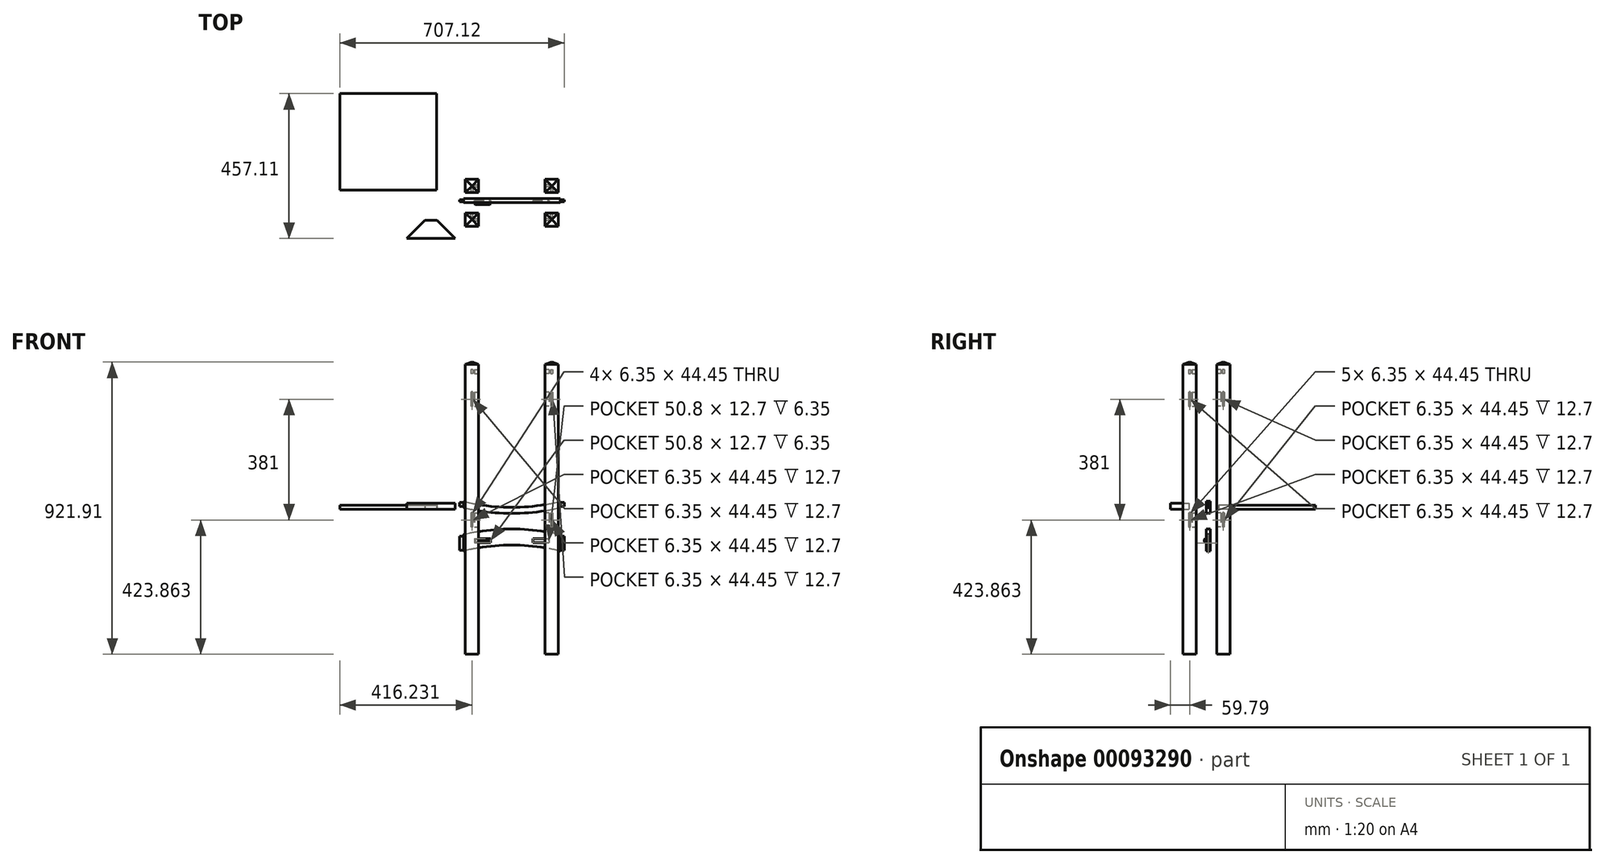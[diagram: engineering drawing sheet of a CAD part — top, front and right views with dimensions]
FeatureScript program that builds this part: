
annotation { "Feature Type Name" : "Feature", "Feature Type Description" : "" }
export const myFeature = defineFeature(function(context is Context, id is Id, definition is map)
    precondition{}
    {
        {
            var Q0;
            Q0=qCreatedBy(makeId("Front.planeOp"),FACE);
            var sketch = newSketch(context, id + "F0", { "sketchPlane" : qUnion([Q0])});
            skLineSegment(sketch, "E0.left", {"start": v(-165.1, 22.23) * mm, "end": v(-165.1, 9.53) * mm});
            skLineSegment(sketch, "E0.right", {"start": v(165.1, 22.23) * mm, "end": v(165.1, 9.53) * mm});
            skLineSegment(sketch, "E1", {"start": v(-152.4, 25.4) * mm, "end": v(-152.4, 22.23) * mm});
            skLineSegment(sketch, "E2", {"start": v(152.4, 25.4) * mm, "end": v(152.4, 22.23) * mm});
            skLineSegment(sketch, "E3.bottom", {"start": v(-165.1, 22.23) * mm, "end": v(-152.4, 22.23) * mm});
            skLineSegment(sketch, "E3.top", {"start": v(-165.1, 9.53) * mm, "end": v(-152.4, 9.53) * mm});
            skLineSegment(sketch, "E4.bottom", {"start": v(165.1, 22.23) * mm, "end": v(152.4, 22.23) * mm});
            skLineSegment(sketch, "E4.top", {"start": v(165.1, 9.53) * mm, "end": v(152.4, 9.53) * mm});
            skLineSegment(sketch, "E5.trimOffspring", {"start": v(-152.4, 9.53) * mm, "end": v(-152.4, 5.76) * mm});
            skPoint(sketch, "E6.orphan", {"position": v(-165.1, -25.4) * mm});
            skLineSegment(sketch, "E7.trimOffspring", {"start": v(152.4, 9.53) * mm, "end": v(152.4, 5.76) * mm});
            skLineSegment(sketch, "E8", {"start": v(-154.76, 6.35) * mm, "end": v(154.76, 6.35) * mm, "construction": true});
            skLineSegment(sketch, "E9", {"start": v(0, 25.4) * mm, "end": v(0, -25.4) * mm, "construction": true});
            skPoint(sketch, "E10", {"position": v(0, 6.35) * mm});
            skArc(sketch, "E11", {"start": v(-152.4, 25.4) * mm, "mid": v(0, 6.35) * mm, "end": v(152.4, 25.4) * mm});
            skArc(sketch, "E12.trimOffspring", {"start": v(-152.4, 5.76) * mm, "mid": v(0, -12.7) * mm, "end": v(152.4, 5.76) * mm});
            skPoint(sketch, "E13.orphan", {"position": v(-152.4, -25.4) * mm});
            skPoint(sketch, "E14.orphan", {"position": v(152.4, -25.4) * mm});
            skSolve(sketch);
        }
        {
            var Q0;
            Q0=qSketchRegion(id+"F0",true);
            extrude(context, id + "F1", {"entities" : qUnion([Q0]), "oppositeDirection" : true, "depth" : 12.7 * mm});
        }
        {
            var Q0;
            Q0=qCreatedBy(makeId("Front.planeOp"),FACE);
            var sketch = newSketch(context, id + "F2", { "sketchPlane" : qUnion([Q0])});
            skLineSegment(sketch, "E15.left", {"start": v(-165.1, -84.02) * mm, "end": v(-165.1, -128.47) * mm});
            skLineSegment(sketch, "E15.right", {"start": v(165.1, -84.02) * mm, "end": v(165.1, -128.47) * mm});
            skLineSegment(sketch, "E16", {"start": v(-152.4, -79.36) * mm, "end": v(-152.4, -84.02) * mm});
            skLineSegment(sketch, "E17", {"start": v(152.4, -79.36) * mm, "end": v(152.4, -84.02) * mm});
            skLineSegment(sketch, "E18", {"start": v(152.4, -84.02) * mm, "end": v(165.1, -84.02) * mm});
            skLineSegment(sketch, "E19", {"start": v(152.4, -128.47) * mm, "end": v(165.1, -128.47) * mm});
            skLineSegment(sketch, "E20", {"start": v(-165.1, -128.47) * mm, "end": v(-152.4, -128.47) * mm});
            skLineSegment(sketch, "E21", {"start": v(-165.1, -84.02) * mm, "end": v(-152.4, -84.02) * mm});
            skPoint(sketch, "E22.orphan", {"position": v(165.1, -131.64) * mm});
            skLineSegment(sketch, "E23.0", {"start": v(-152.4, -112.6) * mm, "end": v(152.4, -112.6) * mm, "construction": true});
            skLineSegment(sketch, "E24", {"start": v(0, -112.6) * mm, "end": v(0, -131.64) * mm, "construction": true});
            skArc(sketch, "E25", {"start": v(152.4, -131.64) * mm, "mid": v(0, -112.6) * mm, "end": v(-152.4, -131.64) * mm});
            skArc(sketch, "E26.0", {"start": v(152.4, -79.36) * mm, "mid": v(0, -61.8) * mm, "end": v(-152.4, -79.36) * mm});
            skLineSegment(sketch, "E27.trimOffspring", {"start": v(-152.4, -128.47) * mm, "end": v(-152.4, -131.64) * mm});
            skLineSegment(sketch, "E28.trimOffspring", {"start": v(152.4, -128.47) * mm, "end": v(152.4, -131.64) * mm});
            skSolve(sketch);
        }
        {
            var Q0;
            Q0=qSketchRegion(id+"F2",true);
            extrude(context, id + "F3", {"entities" : qUnion([Q0]), "oppositeDirection" : true, "depth" : 12.7 * mm});
        }
        {
            var Q0;
            Q0=makeQuery(id+"F3.opExtrude","CAP_FACE",FACE,{"disambiguationData":[OSD([sQuery(id+"F2.wireOp",EDGE,"E15.left"),sQuery(id+"F2.wireOp",EDGE,"E15.right"),sQuery(id+"F2.wireOp",EDGE,"E16"),sQuery(id+"F2.wireOp",EDGE,"E17"),sQuery(id+"F2.wireOp",EDGE,"E18"),sQuery(id+"F2.wireOp",EDGE,"E19"),sQuery(id+"F2.wireOp",EDGE,"E20"),sQuery(id+"F2.wireOp",EDGE,"E21"),sQuery(id+"F2.wireOp",EDGE,"E25"),sQuery(id+"F2.wireOp",EDGE,"E26.0"),sQuery(id+"F2.wireOp",EDGE,"E27.trimOffspring"),sQuery(id+"F2.wireOp",EDGE,"E28.trimOffspring")])],"isStart":true});
            var sketch = newSketch(context, id + "F4", { "sketchPlane" : qUnion([Q0])});
            skLineSegment(sketch, "E29.bottom", {"start": v(-117.47, -91.95) * mm, "end": v(-66.67, -91.95) * mm});
            skLineSegment(sketch, "E29.top", {"start": v(-117.47, -104.65) * mm, "end": v(-66.67, -104.65) * mm});
            skLineSegment(sketch, "E29.left", {"start": v(-117.47, -91.95) * mm, "end": v(-117.47, -104.65) * mm});
            skLineSegment(sketch, "E29.right", {"start": v(-66.67, -91.95) * mm, "end": v(-66.67, -104.65) * mm});
            skPoint(sketch, "E30.oppositeSnap0", {"position": v(-92.07, -104.65) * mm});
            skLineSegment(sketch, "E30.bottom", {"start": v(66.68, -91.95) * mm, "end": v(117.48, -91.95) * mm});
            skLineSegment(sketch, "E30.top", {"start": v(66.68, -104.65) * mm, "end": v(117.48, -104.65) * mm});
            skLineSegment(sketch, "E30.left", {"start": v(66.68, -91.95) * mm, "end": v(66.68, -104.65) * mm});
            skLineSegment(sketch, "E30.right", {"start": v(117.48, -91.95) * mm, "end": v(117.48, -104.65) * mm});
            skSolve(sketch);
        }
        {
            var Q0;
            Q0=qSketchRegion(id+"F4",true);
            extrude(context, id + "F5", {"entities" : qUnion([Q0]), "operationType" : NewBodyOperationType.REMOVE, "oppositeDirection" : true, "depth" : 6.35 * mm});
        }
        {
            var Q0;
            Q0=qCreatedBy(makeId("Top.planeOp"),FACE);
            var sketch = newSketch(context, id + "F6", { "sketchPlane" : qUnion([Q0])});
            skLineSegment(sketch, "E31.bottom", {"start": v(-146.43, -32.48) * mm, "end": v(-105.15, -32.48) * mm});
            skLineSegment(sketch, "E31.top", {"start": v(-146.43, -73.76) * mm, "end": v(-105.15, -73.76) * mm});
            skLineSegment(sketch, "E31.left", {"start": v(-146.43, -32.48) * mm, "end": v(-146.43, -73.76) * mm});
            skLineSegment(sketch, "E31.right", {"start": v(-105.15, -32.48) * mm, "end": v(-105.15, -73.76) * mm});
            skSolve(sketch);
        }
        {
            var Q0;
            Q0=qSketchRegion(id+"F6",true);
            extrude(context, id + "F7", {"entities" : qUnion([Q0]), "endBound" : BoundingType.SYMMETRIC, "depth" : 914.4 * mm});
        }
        {
            var Q0;
            Q0=makeQuery(id+"F7.opExtrude","SWEPT_FACE",FACE,{"disambiguationData":[OSD([sQuery(id+"F6.wireOp",EDGE,"E31.right")])]});
            var sketch = newSketch(context, id + "F8", { "sketchPlane" : qUnion([Q0])});
            skLineSegment(sketch, "E32.bottom", {"start": v(-56.3, 441.33) * mm, "end": v(-49.94, 441.33) * mm});
            skLineSegment(sketch, "E32.top", {"start": v(-56.3, 428.63) * mm, "end": v(-49.94, 428.63) * mm});
            skLineSegment(sketch, "E32.left", {"start": v(-56.3, 441.33) * mm, "end": v(-56.3, 428.63) * mm});
            skLineSegment(sketch, "E32.right", {"start": v(-49.94, 441.33) * mm, "end": v(-49.94, 428.63) * mm});
            skLineSegment(sketch, "E33.bottom", {"start": v(-56.3, 369.89) * mm, "end": v(-49.94, 369.89) * mm});
            skLineSegment(sketch, "E33.top", {"start": v(-56.3, 325.44) * mm, "end": v(-49.94, 325.44) * mm});
            skLineSegment(sketch, "E33.left", {"start": v(-56.3, 369.89) * mm, "end": v(-56.3, 325.44) * mm});
            skLineSegment(sketch, "E33.right", {"start": v(-49.94, 369.89) * mm, "end": v(-49.94, 325.44) * mm});
            skLineSegment(sketch, "E34.bottom", {"start": v(-56.3, -11.11) * mm, "end": v(-49.94, -11.11) * mm});
            skLineSegment(sketch, "E34.top", {"start": v(-56.3, -55.56) * mm, "end": v(-49.94, -55.56) * mm});
            skLineSegment(sketch, "E34.left", {"start": v(-56.3, -11.11) * mm, "end": v(-56.3, -55.56) * mm});
            skLineSegment(sketch, "E34.right", {"start": v(-49.94, -11.11) * mm, "end": v(-49.94, -55.56) * mm});
            skPoint(sketch, "E35", {"position": v(-53.12, 441.33) * mm});
            skSolve(sketch);
        }
        {
            var Q0;
            Q0=makeQuery(id+"F7.opExtrude","CAP_FACE",FACE,{"disambiguationData":[OSD([sQuery(id+"F6.wireOp",EDGE,"E31.bottom"),sQuery(id+"F6.wireOp",EDGE,"E31.top"),sQuery(id+"F6.wireOp",EDGE,"E31.left"),sQuery(id+"F6.wireOp",EDGE,"E31.right")])],"isStart":false});
            extrude(context, id + "F9", {"entities" : qUnion([Q0]), "operationType" : NewBodyOperationType.ADD, "depth" : 7.94 * mm, "hasDraft" : true, "draftAngle" : 70 * degree, "draftPullDirection" : true});
        }
        {
            var Q0;
            Q0=makeQuery(id+"F7.opExtrude","SWEPT_FACE",FACE,{"disambiguationData":[OSD([sQuery(id+"F6.wireOp",EDGE,"E31.bottom")])]});
            var sketch = newSketch(context, id + "F10", { "sketchPlane" : qUnion([Q0])});
            skLineSegment(sketch, "E36.bottom", {"start": v(122.61, 441.33) * mm, "end": v(128.96, 441.33) * mm});
            skLineSegment(sketch, "E36.top", {"start": v(122.61, 428.63) * mm, "end": v(128.96, 428.63) * mm});
            skLineSegment(sketch, "E36.left", {"start": v(122.61, 441.33) * mm, "end": v(122.61, 428.63) * mm});
            skLineSegment(sketch, "E36.right", {"start": v(128.96, 441.33) * mm, "end": v(128.96, 428.63) * mm});
            skLineSegment(sketch, "E37.bottom", {"start": v(122.61, 369.89) * mm, "end": v(128.96, 369.89) * mm});
            skLineSegment(sketch, "E37.top", {"start": v(122.61, 325.44) * mm, "end": v(128.96, 325.44) * mm});
            skLineSegment(sketch, "E37.left", {"start": v(122.61, 369.89) * mm, "end": v(122.61, 325.44) * mm});
            skLineSegment(sketch, "E37.right", {"start": v(128.96, 369.89) * mm, "end": v(128.96, 325.44) * mm});
            skLineSegment(sketch, "E38.bottom", {"start": v(122.61, -11.11) * mm, "end": v(128.96, -11.11) * mm});
            skLineSegment(sketch, "E38.top", {"start": v(122.61, -55.56) * mm, "end": v(128.96, -55.56) * mm});
            skLineSegment(sketch, "E38.left", {"start": v(122.61, -11.11) * mm, "end": v(122.61, -55.56) * mm});
            skLineSegment(sketch, "E38.right", {"start": v(128.96, -11.11) * mm, "end": v(128.96, -55.56) * mm});
            skPoint(sketch, "E39", {"position": v(125.79, 441.33) * mm});
            skLineSegment(sketch, "E40", {"start": v(125.79, 457.2) * mm, "end": v(125.79, 391.14) * mm, "construction": true});
            skSolve(sketch);
        }
        {
            var Q0;
            Q0=makeQuery(id+"F1.opExtrude","CAP_FACE",FACE,{"disambiguationData":[OSD([sQuery(id+"F0.wireOp",EDGE,"E1"),sQuery(id+"F0.wireOp",EDGE,"E2"),sQuery(id+"F0.wireOp",EDGE,"E3.bottom"),sQuery(id+"F0.wireOp",EDGE,"E3.top"),sQuery(id+"F0.wireOp",EDGE,"E0.left"),sQuery(id+"F0.wireOp",EDGE,"E4.bottom"),sQuery(id+"F0.wireOp",EDGE,"E4.top"),sQuery(id+"F0.wireOp",EDGE,"E0.right"),sQuery(id+"F0.wireOp",EDGE,"E5.trimOffspring"),sQuery(id+"F0.wireOp",EDGE,"E7.trimOffspring"),sQuery(id+"F0.wireOp",EDGE,"E11"),sQuery(id+"F0.wireOp",EDGE,"E12.trimOffspring")])],"isStart":true});
            var sketch = newSketch(context, id + "F11", { "sketchPlane" : qUnion([Q0])});
            skLineSegment(sketch, "E41", {"start": v(152.4, 22.23) * mm, "end": v(152.4, 9.53) * mm});
            skLineSegment(sketch, "E42", {"start": v(-152.4, 22.23) * mm, "end": v(-152.4, 9.53) * mm});
            skSolve(sketch);
        }
        {
            var Q0;
            Q0=qSketchRegion(id+"F10",true);
            extrude(context, id + "F12", {"entities" : qUnion([Q0]), "operationType" : NewBodyOperationType.REMOVE, "oppositeDirection" : true, "depth" : 12.7 * mm});
        }
        {
            var Q0;
            Q0=makeQuery(id+"F11.imprint","IMPRINT",FACE,{"disambiguationData":[TD([[makeQuery(id+"F11.imprint","IMPRINT",EDGE,{"derivedFrom":sQuery(id+"F11.wireOp",EDGE,"E42")}),-1.0]])]});
            var Q1;
            Q1=makeQuery(id+"F11.imprint","IMPRINT",FACE,{"disambiguationData":[TD([[makeQuery(id+"F11.imprint","IMPRINT",EDGE,{"derivedFrom":sQuery(id+"F11.wireOp",EDGE,"E41")}),1.0]])]});
            extrude(context, id + "F13", {"entities" : qUnion([Q0, Q1]), "operationType" : NewBodyOperationType.REMOVE, "oppositeDirection" : true, "depth" : 3.17 * mm});
        }
        {
            var Q0;
            Q0=makeQuery(id+"F1.opExtrude","CAP_FACE",FACE,{"disambiguationData":[OSD([sQuery(id+"F0.wireOp",EDGE,"E1"),sQuery(id+"F0.wireOp",EDGE,"E2"),sQuery(id+"F0.wireOp",EDGE,"E3.bottom"),sQuery(id+"F0.wireOp",EDGE,"E3.top"),sQuery(id+"F0.wireOp",EDGE,"E0.left"),sQuery(id+"F0.wireOp",EDGE,"E4.bottom"),sQuery(id+"F0.wireOp",EDGE,"E4.top"),sQuery(id+"F0.wireOp",EDGE,"E0.right"),sQuery(id+"F0.wireOp",EDGE,"E5.trimOffspring"),sQuery(id+"F0.wireOp",EDGE,"E7.trimOffspring"),sQuery(id+"F0.wireOp",EDGE,"E11"),sQuery(id+"F0.wireOp",EDGE,"E12.trimOffspring")])],"isStart":false});
            var sketch = newSketch(context, id + "F14", { "sketchPlane" : qUnion([Q0])});
            skLineSegment(sketch, "E43", {"start": v(-152.4, 22.23) * mm, "end": v(-152.4, 9.53) * mm});
            skLineSegment(sketch, "E44", {"start": v(152.4, 22.23) * mm, "end": v(152.4, 9.53) * mm});
            skSolve(sketch);
        }
        {
            var Q0;
            Q0=makeQuery(id+"F14.imprint","IMPRINT",FACE,{"disambiguationData":[TD([[makeQuery(id+"F14.imprint","IMPRINT",EDGE,{"derivedFrom":sQuery(id+"F14.wireOp",EDGE,"E43")}),-1.0]])]});
            var Q1;
            Q1=makeQuery(id+"F14.imprint","IMPRINT",FACE,{"disambiguationData":[TD([[makeQuery(id+"F14.imprint","IMPRINT",EDGE,{"derivedFrom":sQuery(id+"F14.wireOp",EDGE,"E44")}),1.0]])]});
            extrude(context, id + "F15", {"entities" : qUnion([Q0, Q1]), "operationType" : NewBodyOperationType.REMOVE, "oppositeDirection" : true, "depth" : 3.17 * mm});
        }
        {
            var Q0;
            Q0=makeQuery(id+"F3.opExtrude","CAP_FACE",FACE,{"disambiguationData":[OSD([sQuery(id+"F2.wireOp",EDGE,"E15.left"),sQuery(id+"F2.wireOp",EDGE,"E15.right"),sQuery(id+"F2.wireOp",EDGE,"E16"),sQuery(id+"F2.wireOp",EDGE,"E17"),sQuery(id+"F2.wireOp",EDGE,"E18"),sQuery(id+"F2.wireOp",EDGE,"E19"),sQuery(id+"F2.wireOp",EDGE,"E20"),sQuery(id+"F2.wireOp",EDGE,"E21"),sQuery(id+"F2.wireOp",EDGE,"E25"),sQuery(id+"F2.wireOp",EDGE,"E26.0"),sQuery(id+"F2.wireOp",EDGE,"E27.trimOffspring"),sQuery(id+"F2.wireOp",EDGE,"E28.trimOffspring")])],"isStart":false});
            var sketch = newSketch(context, id + "F16", { "sketchPlane" : qUnion([Q0])});
            skLineSegment(sketch, "E45", {"start": v(-152.4, -84.02) * mm, "end": v(-152.4, -128.47) * mm});
            skLineSegment(sketch, "E46", {"start": v(152.4, -84.02) * mm, "end": v(152.4, -128.47) * mm});
            skSolve(sketch);
        }
        {
            var Q0;
            Q0=makeQuery(id+"F16.imprint","IMPRINT",FACE,{"disambiguationData":[TD([[makeQuery(id+"F16.imprint","IMPRINT",EDGE,{"derivedFrom":sQuery(id+"F16.wireOp",EDGE,"E45")}),-1.0]])]});
            var Q1;
            Q1=makeQuery(id+"F16.imprint","IMPRINT",FACE,{"disambiguationData":[TD([[makeQuery(id+"F16.imprint","IMPRINT",EDGE,{"derivedFrom":sQuery(id+"F16.wireOp",EDGE,"E46")}),1.0]])]});
            extrude(context, id + "F17", {"entities" : qUnion([Q0, Q1]), "operationType" : NewBodyOperationType.REMOVE, "oppositeDirection" : true, "depth" : 3.17 * mm});
        }
        {
            var Q0;
            Q0=makeQuery(id+"F3.opExtrude","CAP_FACE",FACE,{"disambiguationData":[OSD([sQuery(id+"F2.wireOp",EDGE,"E15.left"),sQuery(id+"F2.wireOp",EDGE,"E15.right"),sQuery(id+"F2.wireOp",EDGE,"E16"),sQuery(id+"F2.wireOp",EDGE,"E17"),sQuery(id+"F2.wireOp",EDGE,"E18"),sQuery(id+"F2.wireOp",EDGE,"E19"),sQuery(id+"F2.wireOp",EDGE,"E20"),sQuery(id+"F2.wireOp",EDGE,"E21"),sQuery(id+"F2.wireOp",EDGE,"E25"),sQuery(id+"F2.wireOp",EDGE,"E26.0"),sQuery(id+"F2.wireOp",EDGE,"E27.trimOffspring"),sQuery(id+"F2.wireOp",EDGE,"E28.trimOffspring")])],"isStart":true});
            var sketch = newSketch(context, id + "F18", { "sketchPlane" : qUnion([Q0])});
            skLineSegment(sketch, "E47", {"start": v(-152.4, -84.02) * mm, "end": v(-152.4, -128.47) * mm});
            skLineSegment(sketch, "E48", {"start": v(152.4, -84.02) * mm, "end": v(152.4, -128.47) * mm});
            skSolve(sketch);
        }
        {
            var Q0;
            Q0=makeQuery(id+"F18.imprint","IMPRINT",FACE,{"disambiguationData":[TD([[makeQuery(id+"F18.imprint","IMPRINT",EDGE,{"derivedFrom":sQuery(id+"F18.wireOp",EDGE,"E47")}),-1.0]])]});
            var Q1;
            Q1=makeQuery(id+"F18.imprint","IMPRINT",FACE,{"disambiguationData":[TD([[makeQuery(id+"F18.imprint","IMPRINT",EDGE,{"derivedFrom":sQuery(id+"F18.wireOp",EDGE,"E48")}),1.0]])]});
            extrude(context, id + "F19", {"entities" : qUnion([Q0, Q1]), "operationType" : NewBodyOperationType.REMOVE, "oppositeDirection" : true, "depth" : 3.17 * mm});
        }
        {
            var Q0;
            Q0=qSketchRegion(id+"F8",true);
            extrude(context, id + "F20", {"entities" : qUnion([Q0]), "operationType" : NewBodyOperationType.REMOVE, "oppositeDirection" : true, "depth" : 12.7 * mm});
        }
        {
            var Q0;
            Q0=makeQuery(id+"F7.opExtrude","SWEPT_BODY",BODY,{"disambiguationData":[OSD([sQuery(id+"F6.wireOp",EDGE,"E31.bottom"),sQuery(id+"F6.wireOp",EDGE,"E31.top"),sQuery(id+"F6.wireOp",EDGE,"E31.left"),sQuery(id+"F6.wireOp",EDGE,"E31.right")])]});
            var Q1;
            Q1=qCreatedBy(makeId("Right.planeOp"),FACE);
            mirror(context, id + "F21", {"entities" : qUnion([Q0]), "mirrorPlane" : qUnion([Q1])});
        }
        {
            var Q0;
            Q0=makeQuery(id+"F21.opPattern","COPY",BODY,{"derivedFrom":makeQuery(id+"F7.opExtrude","SWEPT_BODY",BODY,{"disambiguationData":[OSD([sQuery(id+"F6.wireOp",EDGE,"E31.bottom"),sQuery(id+"F6.wireOp",EDGE,"E31.top"),sQuery(id+"F6.wireOp",EDGE,"E31.left"),sQuery(id+"F6.wireOp",EDGE,"E31.right")])]}),"instanceName":"1"});
            var Q1;
            Q1=makeQuery(id+"F7.opExtrude","SWEPT_BODY",BODY,{"disambiguationData":[OSD([sQuery(id+"F6.wireOp",EDGE,"E31.bottom"),sQuery(id+"F6.wireOp",EDGE,"E31.top"),sQuery(id+"F6.wireOp",EDGE,"E31.left"),sQuery(id+"F6.wireOp",EDGE,"E31.right")])]});
            var Q2;
            Q2=qCreatedBy(makeId("Front.planeOp"),FACE);
            mirror(context, id + "F22", {"entities" : qUnion([Q0, Q1]), "mirrorPlane" : qUnion([Q2])});
        }
        {
            var Q0;
            Q0=makeQuery(id+"F5.boolean.opBoolean","COPY",FACE,{"derivedFrom":makeQuery(id+"F5.opExtrude","CAP_FACE",FACE,{"disambiguationData":[OSD([sQuery(id+"F4.wireOp",EDGE,"E29.bottom"),sQuery(id+"F4.wireOp",EDGE,"E29.top"),sQuery(id+"F4.wireOp",EDGE,"E29.left"),sQuery(id+"F4.wireOp",EDGE,"E29.right")])],"isStart":false})});
            var sketch = newSketch(context, id + "F23", { "sketchPlane" : qUnion([Q0])});
            skLineSegment(sketch, "E49.0", {"start": v(-117.47, -91.95) * mm, "end": v(-66.67, -91.95) * mm});
            skLineSegment(sketch, "E49.1", {"start": v(66.68, -91.95) * mm, "end": v(117.48, -91.95) * mm});
            skLineSegment(sketch, "E50", {"start": v(-117.47, -91.95) * mm, "end": v(-117.47, -104.65) * mm});
            skLineSegment(sketch, "E51", {"start": v(-117.47, -104.65) * mm, "end": v(-66.67, -104.65) * mm});
            skLineSegment(sketch, "E52", {"start": v(-66.67, -104.65) * mm, "end": v(-66.67, -91.95) * mm});
            skLineSegment(sketch, "E53", {"start": v(66.68, -91.95) * mm, "end": v(66.68, -104.65) * mm});
            skLineSegment(sketch, "E54", {"start": v(66.68, -104.65) * mm, "end": v(117.48, -104.65) * mm});
            skLineSegment(sketch, "E55", {"start": v(117.48, -104.65) * mm, "end": v(117.48, -91.95) * mm});
            skSolve(sketch);
        }
        {
            var Q0;
            Q0=qSketchRegion(id+"F23",true);
            extrude(context, id + "F24", {"entities" : qUnion([Q0]), "depth" : 12.7 * mm});
        }
        {
            var Q0;
            Q0=makeQuery(id+"F24.opExtrude","CAP_EDGE",EDGE,{"disambiguationData":[OSD([sQuery(id+"F23.wireOp",EDGE,"E49.0")])],"isStart":false});
            var Q1;
            Q1=makeQuery(id+"F24.opExtrude","CAP_EDGE",EDGE,{"disambiguationData":[OSD([sQuery(id+"F23.wireOp",EDGE,"E50")])],"isStart":false});
            var Q2;
            Q2=makeQuery(id+"F24.opExtrude","CAP_EDGE",EDGE,{"disambiguationData":[OSD([sQuery(id+"F23.wireOp",EDGE,"E51")])],"isStart":false});
            var Q3;
            Q3=makeQuery(id+"F24.opExtrude","CAP_EDGE",EDGE,{"disambiguationData":[OSD([sQuery(id+"F23.wireOp",EDGE,"E52")])],"isStart":false});
            chamfer(context, id + "F25", {"entities" : qUnion([Q0, Q1, Q2, Q3]), "width" : 2.54 * mm, "tangentPropagation" : true});
        }
        {
            var Q0;
            Q0=makeQuery(id+"F24.opExtrude","CAP_EDGE",EDGE,{"disambiguationData":[OSD([sQuery(id+"F23.wireOp",EDGE,"E49.1")])],"isStart":false});
            var Q1;
            Q1=makeQuery(id+"F24.opExtrude","CAP_EDGE",EDGE,{"disambiguationData":[OSD([sQuery(id+"F23.wireOp",EDGE,"E53")])],"isStart":false});
            var Q2;
            Q2=makeQuery(id+"F24.opExtrude","CAP_EDGE",EDGE,{"disambiguationData":[OSD([sQuery(id+"F23.wireOp",EDGE,"E54")])],"isStart":false});
            var Q3;
            Q3=makeQuery(id+"F24.opExtrude","CAP_EDGE",EDGE,{"disambiguationData":[OSD([sQuery(id+"F23.wireOp",EDGE,"E55")])],"isStart":false});
            chamfer(context, id + "F26", {"entities" : qUnion([Q0, Q1, Q2, Q3]), "width" : 2.54 * mm, "tangentPropagation" : true});
        }
        {
            var Q0;
            Q0=makeQuery(id+"F24.opExtrude","SWEPT_BODY",BODY,{"disambiguationData":[OSD([sQuery(id+"F23.wireOp",EDGE,"E49.1"),sQuery(id+"F23.wireOp",EDGE,"E53"),sQuery(id+"F23.wireOp",EDGE,"E54"),sQuery(id+"F23.wireOp",EDGE,"E55")])]});
            deleteBodies(context, id + "F27", {"entities" : qUnion([Q0])});
        }
        {
            var Q0;
            Q0=qCreatedBy(makeId("Top.planeOp"),FACE);
            var sketch = newSketch(context, id + "F28", { "sketchPlane" : qUnion([Q0])});
            skLineSegment(sketch, "E56.bottom", {"start": v(-331.28, -112.91) * mm, "end": v(-178.88, -112.91) * mm});
            skLineSegment(sketch, "E56.top", {"start": v(-274.13, -55.76) * mm, "end": v(-236.03, -55.76) * mm});
            skLineSegment(sketch, "E57", {"start": v(-331.28, -112.91) * mm, "end": v(-274.13, -55.76) * mm});
            skLineSegment(sketch, "E58", {"start": v(-178.88, -112.91) * mm, "end": v(-236.03, -55.76) * mm});
            skSolve(sketch);
        }
        {
            var Q0;
            Q0=makeQuery(id+"F28.imprint","IMPRINT",FACE,{"disambiguationData":[TD([[makeQuery(id+"F28.imprint","IMPRINT",EDGE,{"derivedFrom":sQuery(id+"F28.wireOp",EDGE,"E56.bottom")}),1.0]])]});
            extrude(context, id + "F29", {"entities" : qUnion([Q0]), "depth" : 19.05 * mm});
        }
        {
            var Q0;
            Q0=qCreatedBy(makeId("Top.planeOp"),FACE);
            var sketch = newSketch(context, id + "F30", { "sketchPlane" : qUnion([Q0])});
            skLineSegment(sketch, "E59.bottom", {"start": v(-542.02, 344.2) * mm, "end": v(-237.22, 344.2) * mm});
            skLineSegment(sketch, "E59.top", {"start": v(-542.02, 39.4) * mm, "end": v(-237.22, 39.4) * mm});
            skLineSegment(sketch, "E59.left", {"start": v(-542.02, 344.2) * mm, "end": v(-542.02, 39.4) * mm});
            skLineSegment(sketch, "E59.right", {"start": v(-237.22, 344.2) * mm, "end": v(-237.22, 39.4) * mm});
            skSolve(sketch);
        }
        {
            var Q0;
            Q0=makeQuery(id+"F30.imprint","IMPRINT",FACE,{"disambiguationData":[TD([[makeQuery(id+"F30.imprint","IMPRINT",EDGE,{"derivedFrom":sQuery(id+"F30.wireOp",EDGE,"E59.bottom")}),-1.0]])]});
            extrude(context, id + "F31", {"entities" : qUnion([Q0]), "depth" : 12.7 * mm});
        }
    });
